# Revit family: Detail-Bolt Assembly-ISO Metric-Hexagon-Top
name_source: partatom
category: Detail Items
revit_build: Autodesk Revit 2018 (Build: 20170927_1515(x64)
units: mm (PartAtom-declared; Revit-internal decimal feet)

## family parameters
OmniClass Number = 23.20.40.11.14.27
OmniClass Title = Bolts and Nuts
Rotate with component = No
Section Shape = Not Defined
Shared = No

## types (12) — shared parameters
CBICode = 3411
CBIDescription = Structural steelwork
Description = ISO Metric Precision Hexagon Bolt in accordance with BS 3692:2001
Manufacturer = Steel & Tube
ManufacturerName = Steel & Tube
ManufacturerURL = http://www.steelandtube.co.nz
ModifiedIssue_ANZRS = 20160520 $
SpecificationDescription = Steel & Tube Purlins & Girts
SpecificationReference = 3411ST
Type Comments = Top View
URL = http://www.steelandtube.co.nz
Uniclass2015Code = Pr_20_76_51_21
Uniclass2015Title = Cold-formed galvanized steel sections
Uniclass2015Version = 2015

## per-type parameters (varying)
| type | Bolt Diameter | Centreline Size | Nut Size |
| M3 | 3 mm  [stored 0.00984252 ft] | 11 mm | 5.5 mm  [stored 0.0180446 ft] |
| M4 | 4 mm  [stored 0.0131234 ft] | 14 mm  [stored 0.0459318 ft] | 7 mm  [stored 0.0229659 ft] |
| M5 | 5 mm  [stored 0.0164042 ft] | 16 mm  [stored 0.0524934 ft] | 8 mm  [stored 0.0262467 ft] |
| M6 | 6 mm  [stored 0.019685 ft] | 20 mm  [stored 0.0656168 ft] | 10 mm  [stored 0.0328084 ft] |
| M8 | 8 mm  [stored 0.0262467 ft] | 26 mm | 13 mm |
| M10 | 10 mm  [stored 0.0328084 ft] | 34 mm | 17 mm |
| M12 | 12 mm  [stored 0.0393701 ft] | 38 mm | 19 mm  [stored 0.062336 ft] |
| M16 | 16 mm  [stored 0.0524934 ft] | 48 mm  [stored 0.15748 ft] | 24 mm  [stored 0.0787402 ft] |
| M20 | 20 mm  [stored 0.0656168 ft] | 60 mm | 30 mm  [stored 0.0984252 ft] |
| M24 | 24 mm  [stored 0.0787402 ft] | 72 mm | 36 mm  [stored 0.11811 ft] |
| M30 | 30 mm  [stored 0.0984252 ft] | 92 mm | 46 mm  [stored 0.150919 ft] |
| M36 | 36 mm  [stored 0.11811 ft] | 110 mm | 55 mm  [stored 0.180446 ft] |

note: column(s) folded — value = type name in every type: Model

note: [stored X ft] marks values corroborated as IEEE doubles in the binary element streams (Revit-internal decimal feet)

## geometry (parser evidence)
native form markers: Sweep x1
no freeform markers — native parametric forms only
